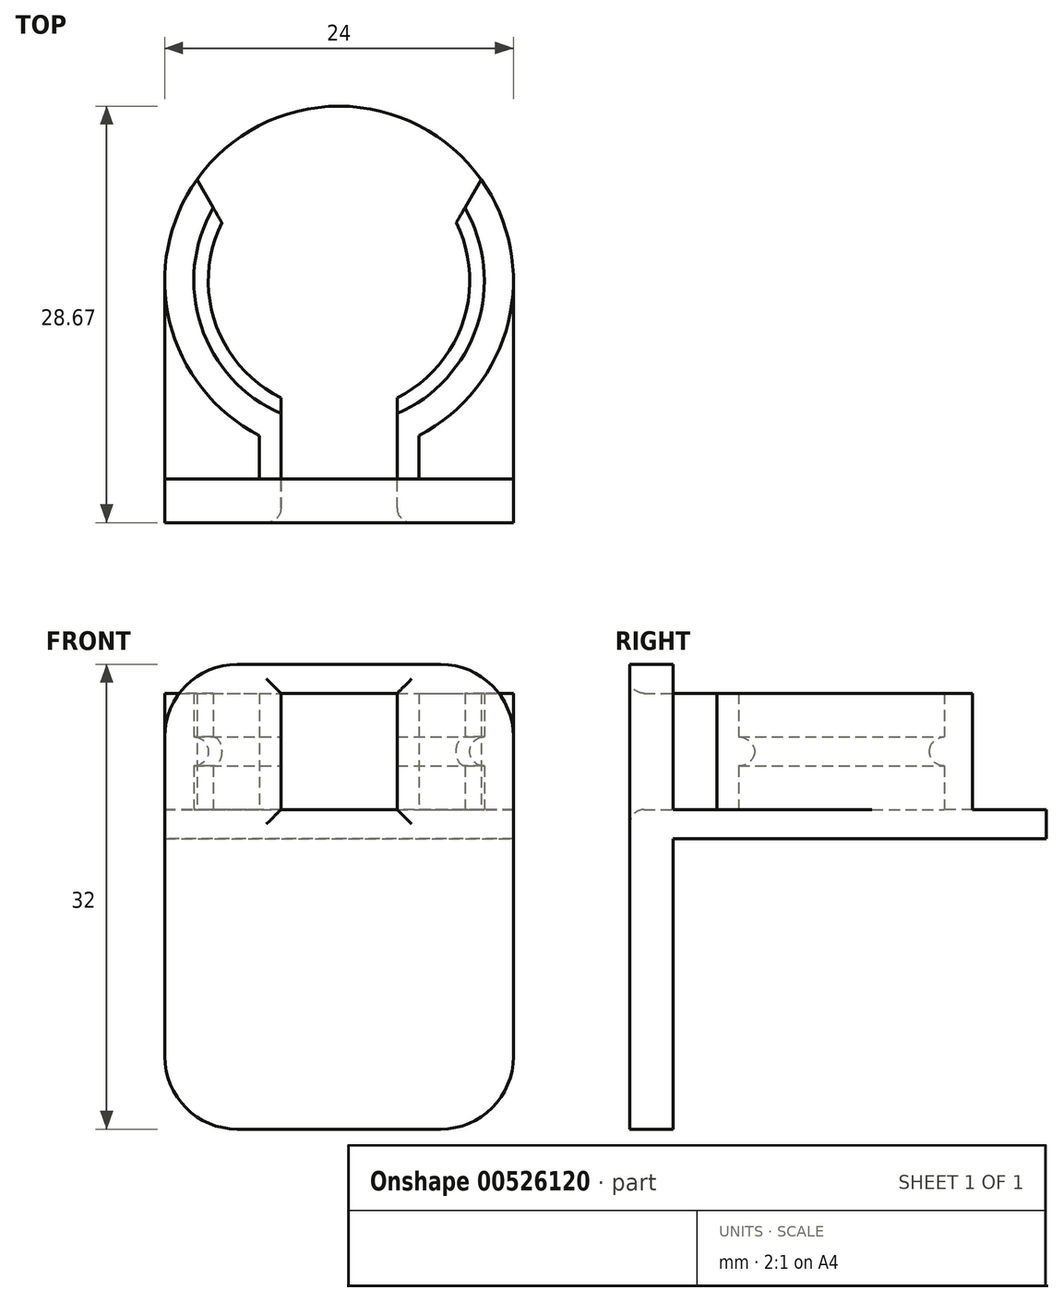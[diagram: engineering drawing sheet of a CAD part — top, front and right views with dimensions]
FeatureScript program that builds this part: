
annotation { "Feature Type Name" : "Feature", "Feature Type Description" : "" }
export const myFeature = defineFeature(function(context is Context, id is Id, definition is map)
    precondition{}
    {
        {
            var Q0;
            Q0=qCreatedBy(makeId("Top.planeOp"),FACE);
            var sketch = newSketch(context, id + "F0", { "sketchPlane" : qUnion([Q0])});
            skArc(sketch, "E0", {"start": v(-5.5, 1.5) * mm, "mid": v(0, 24.17) * mm, "end": v(5.5, 1.5) * mm});
            skArc(sketch, "E1", {"start": v(-5.5, -1.5) * mm, "mid": v(0, -24.17) * mm, "end": v(5.5, -1.5) * mm});
            skLineSegment(sketch, "E2", {"start": v(-5.5, 1.5) * mm, "end": v(-5.5, -1.5) * mm});
            skLineSegment(sketch, "E3", {"start": v(5.5, 1.5) * mm, "end": v(5.5, -1.5) * mm});
            skSolve(sketch);
        }
        {
            var Q0;
            Q0=qSketchRegion(id+"F0",true);
            extrude(context, id + "F1", {"entities" : qUnion([Q0]), "depth" : 2 * mm, "offsetDistance" : 25 * mm});
        }
        {
            var Q0;
            Q0=makeQuery(id+"F1.opExtrude","CAP_FACE",FACE,{"disambiguationData":[OSD([sQuery(id+"F0.wireOp",EDGE,"E0"),sQuery(id+"F0.wireOp",EDGE,"E1"),sQuery(id+"F0.wireOp",EDGE,"E2"),sQuery(id+"F0.wireOp",EDGE,"E3")])],"isStart":false});
            var sketch = newSketch(context, id + "F2", { "sketchPlane" : qUnion([Q0])});
            skArc(sketch, "E4", {"start": v(8.66, 17.17) * mm, "mid": v(9.5, 9.04) * mm, "end": v(4, 3) * mm});
            skArc(sketch, "E5", {"start": v(9.78, 19.11) * mm, "mid": v(11.66, 9.33) * mm, "end": v(5.5, 1.5) * mm});
            skArc(sketch, "E6", {"start": v(-8.66, 17.17) * mm, "mid": v(-9.5, 9.04) * mm, "end": v(-4, 3) * mm});
            skArc(sketch, "E7", {"start": v(5.5, -3.81) * mm, "mid": v(9.59, -9.32) * mm, "end": v(9.17, -16.17) * mm});
            skLineSegment(sketch, "E8", {"start": v(9.78, 19.11) * mm, "end": v(8.66, 17.17) * mm});
            skLineSegment(sketch, "E9", {"start": v(-8.66, 17.17) * mm, "end": v(-9.78, 19.11) * mm});
            skLineSegment(sketch, "E10", {"start": v(5.5, 1.5) * mm, "end": v(5.5, -3.81) * mm});
            skLineSegment(sketch, "E11", {"start": v(-4, 3) * mm, "end": v(-4, -6.24) * mm});
            skLineSegment(sketch, "E12", {"start": v(-4, -6.24) * mm, "end": v(-9.17, -16.17) * mm});
            skLineSegment(sketch, "E13", {"start": v(9.17, -16.17) * mm, "end": v(4, -6.24) * mm});
            skLineSegment(sketch, "E14", {"start": v(4, -6.24) * mm, "end": v(4, 3) * mm});
            skArc(sketch, "E15", {"start": v(-9.78, 19.11) * mm, "mid": v(-11.66, 9.33) * mm, "end": v(-5.5, 1.5) * mm});
            skArc(sketch, "E16", {"start": v(-9.17, -16.17) * mm, "mid": v(-9.59, -9.32) * mm, "end": v(-5.5, -3.81) * mm});
            skLineSegment(sketch, "E17", {"start": v(-5.5, 1.5) * mm, "end": v(-5.5, -3.81) * mm});
            skArc(sketch, "E18.0", {"start": v(-5.5, 1.5) * mm, "mid": v(0, 24.17) * mm, "end": v(5.5, 1.5) * mm, "construction": true});
            skArc(sketch, "E19.0", {"start": v(-5.5, -1.5) * mm, "mid": v(0, -24.17) * mm, "end": v(5.5, -1.5) * mm, "construction": true});
            skSolve(sketch);
        }
        {
            var Q0;
            Q0=qSketchRegion(id+"F2",true);
            extrude(context, id + "F3", {"entities" : qUnion([Q0]), "operationType" : NewBodyOperationType.ADD, "depth" : 3 * mm, "offsetDistance" : 25 * mm});
        }
        {
            var Q0;
            Q0=makeQuery(id+"F3.opExtrude","CAP_FACE",FACE,{"disambiguationData":[OSD([sQuery(id+"F2.wireOp",EDGE,"E4"),sQuery(id+"F2.wireOp",EDGE,"E5"),sQuery(id+"F2.wireOp",EDGE,"E7"),sQuery(id+"F2.wireOp",EDGE,"E8"),sQuery(id+"F2.wireOp",EDGE,"E10"),sQuery(id+"F2.wireOp",EDGE,"E13"),sQuery(id+"F2.wireOp",EDGE,"E14")])],"isStart":false});
            var sketch = newSketch(context, id + "F4", { "sketchPlane" : qUnion([Q0])});
            skArc(sketch, "E20", {"start": v(-9.78, 19.11) * mm, "mid": v(-11.66, 9.33) * mm, "end": v(-5.5, 1.5) * mm});
            skArc(sketch, "E21", {"start": v(9.78, 19.11) * mm, "mid": v(11.66, 9.33) * mm, "end": v(5.5, 1.5) * mm});
            skArc(sketch, "E22", {"start": v(8.07, 16.15) * mm, "mid": v(8.53, 9.28) * mm, "end": v(4, 4.1) * mm});
            skArc(sketch, "E23", {"start": v(-8.07, 16.15) * mm, "mid": v(-8.53, 9.28) * mm, "end": v(-4, 4.1) * mm});
            skArc(sketch, "E24", {"start": v(5.5, -5.04) * mm, "mid": v(8.6, -9.53) * mm, "end": v(8.55, -14.98) * mm});
            skArc(sketch, "E25", {"start": v(-5.5, -5.04) * mm, "mid": v(-8.6, -9.53) * mm, "end": v(-8.55, -14.98) * mm});
            skLineSegment(sketch, "E26", {"start": v(-5.5, 1.5) * mm, "end": v(-5.5, -5.04) * mm});
            skLineSegment(sketch, "E27", {"start": v(5.5, 1.5) * mm, "end": v(5.5, -5.04) * mm});
            skLineSegment(sketch, "E28", {"start": v(-4, 4.1) * mm, "end": v(-4, -6.24) * mm});
            skLineSegment(sketch, "E29", {"start": v(-4, -6.24) * mm, "end": v(-8.55, -14.98) * mm});
            skLineSegment(sketch, "E30", {"start": v(4, 4.1) * mm, "end": v(4, -6.24) * mm});
            skLineSegment(sketch, "E31", {"start": v(4, -6.24) * mm, "end": v(8.55, -14.98) * mm});
            skLineSegment(sketch, "E32", {"start": v(8.07, 16.15) * mm, "end": v(9.78, 19.11) * mm});
            skLineSegment(sketch, "E33", {"start": v(-9.78, 19.11) * mm, "end": v(-8.07, 16.15) * mm});
            skLineSegment(sketch, "E34.0", {"start": v(-8.66, 17.17) * mm, "end": v(-9.78, 19.11) * mm, "construction": true});
            skLineSegment(sketch, "E35.0", {"start": v(9.78, 19.11) * mm, "end": v(8.66, 17.17) * mm, "construction": true});
            skLineSegment(sketch, "E36.0", {"start": v(-4, -6.24) * mm, "end": v(-9.17, -16.17) * mm, "construction": true});
            skLineSegment(sketch, "E37.0", {"start": v(9.17, -16.17) * mm, "end": v(4, -6.24) * mm, "construction": true});
            skArc(sketch, "E38.0", {"start": v(-9.78, 19.11) * mm, "mid": v(0, 24.17) * mm, "end": v(9.78, 19.11) * mm, "construction": true});
            skArc(sketch, "E39.0", {"start": v(-5.5, -1.5) * mm, "mid": v(0, -24.17) * mm, "end": v(5.5, -1.5) * mm, "construction": true});
            skSolve(sketch);
        }
        {
            var Q0;
            Q0=qSketchRegion(id+"F4",true);
            extrude(context, id + "F5", {"entities" : qUnion([Q0]), "operationType" : NewBodyOperationType.ADD, "depth" : 2 * mm, "offsetDistance" : 25 * mm});
        }
        {
            var Q0;
            Q0=makeQuery(id+"F5.opExtrude","CAP_FACE",FACE,{"disambiguationData":[OSD([sQuery(id+"F4.wireOp",EDGE,"E21"),sQuery(id+"F4.wireOp",EDGE,"E22"),sQuery(id+"F4.wireOp",EDGE,"E24"),sQuery(id+"F4.wireOp",EDGE,"E27"),sQuery(id+"F4.wireOp",EDGE,"E30"),sQuery(id+"F4.wireOp",EDGE,"E31"),sQuery(id+"F4.wireOp",EDGE,"E32")])],"isStart":false});
            var sketch = newSketch(context, id + "F6", { "sketchPlane" : qUnion([Q0])});
            skArc(sketch, "E40", {"start": v(8.66, 17.17) * mm, "mid": v(9.5, 9.04) * mm, "end": v(4, 3) * mm});
            skArc(sketch, "E41", {"start": v(9.78, 19.11) * mm, "mid": v(11.66, 9.33) * mm, "end": v(5.5, 1.5) * mm});
            skArc(sketch, "E42", {"start": v(-8.66, 17.17) * mm, "mid": v(-9.5, 9.04) * mm, "end": v(-4, 3) * mm});
            skArc(sketch, "E43", {"start": v(5.5, -3.81) * mm, "mid": v(9.59, -9.32) * mm, "end": v(9.17, -16.17) * mm});
            skLineSegment(sketch, "E44", {"start": v(9.78, 19.11) * mm, "end": v(8.66, 17.17) * mm});
            skLineSegment(sketch, "E45", {"start": v(-8.66, 17.17) * mm, "end": v(-9.78, 19.11) * mm});
            skLineSegment(sketch, "E46", {"start": v(5.5, 1.5) * mm, "end": v(5.5, -3.81) * mm});
            skLineSegment(sketch, "E47", {"start": v(-4, 3) * mm, "end": v(-4, -6.24) * mm});
            skLineSegment(sketch, "E48", {"start": v(-4, -6.24) * mm, "end": v(-9.17, -16.17) * mm});
            skLineSegment(sketch, "E49", {"start": v(9.17, -16.17) * mm, "end": v(4, -6.24) * mm});
            skLineSegment(sketch, "E50", {"start": v(4, -6.24) * mm, "end": v(4, 3) * mm});
            skArc(sketch, "E51", {"start": v(-9.78, 19.11) * mm, "mid": v(-11.66, 9.33) * mm, "end": v(-5.5, 1.5) * mm});
            skArc(sketch, "E52", {"start": v(-9.17, -16.17) * mm, "mid": v(-9.59, -9.32) * mm, "end": v(-5.5, -3.81) * mm});
            skLineSegment(sketch, "E53", {"start": v(-5.5, 1.5) * mm, "end": v(-5.5, -3.81) * mm});
            skArc(sketch, "E54.0", {"start": v(-5.5, -1.5) * mm, "mid": v(0, -24.17) * mm, "end": v(5.5, -1.5) * mm, "construction": true});
            skArc(sketch, "E55.0", {"start": v(-9.78, 19.11) * mm, "mid": v(0, 24.17) * mm, "end": v(9.78, 19.11) * mm, "construction": true});
            skSolve(sketch);
        }
        {
            var Q0;
            Q0=qSketchRegion(id+"F6",true);
            extrude(context, id + "F7", {"entities" : qUnion([Q0]), "operationType" : NewBodyOperationType.ADD, "depth" : 3 * mm, "offsetDistance" : 25 * mm});
        }
        {
            var Q0;
            Q0=makeQuery(id+"F5.opExtrude","CAP_EDGE",EDGE,{"disambiguationData":[OSD([sQuery(id+"F4.wireOp",EDGE,"E22")])],"isStart":false});
            var Q1;
            Q1=makeQuery(id+"F5.opExtrude","CAP_EDGE",EDGE,{"disambiguationData":[OSD([sQuery(id+"F4.wireOp",EDGE,"E23")])],"isStart":false});
            var Q2;
            Q2=makeQuery(id+"F5.opExtrude","CAP_EDGE",EDGE,{"disambiguationData":[OSD([sQuery(id+"F4.wireOp",EDGE,"E23")])],"isStart":true});
            var Q3;
            Q3=makeQuery(id+"F5.opExtrude","CAP_EDGE",EDGE,{"disambiguationData":[OSD([sQuery(id+"F4.wireOp",EDGE,"E22")])],"isStart":true});
            var Q4;
            Q4=makeQuery(id+"F5.opExtrude","CAP_EDGE",EDGE,{"disambiguationData":[OSD([sQuery(id+"F4.wireOp",EDGE,"E25")])],"isStart":true});
            var Q5;
            Q5=makeQuery(id+"F5.opExtrude","CAP_EDGE",EDGE,{"disambiguationData":[OSD([sQuery(id+"F4.wireOp",EDGE,"E25")])],"isStart":false});
            var Q6;
            Q6=makeQuery(id+"F5.opExtrude","CAP_EDGE",EDGE,{"disambiguationData":[OSD([sQuery(id+"F4.wireOp",EDGE,"E24")])],"isStart":false});
            var Q7;
            Q7=makeQuery(id+"F5.opExtrude","CAP_EDGE",EDGE,{"disambiguationData":[OSD([sQuery(id+"F4.wireOp",EDGE,"E24")])],"isStart":true});
            fillet(context, id + "F8", {"entities" : qUnion([Q0, Q1, Q2, Q3, Q4, Q5, Q6, Q7]), "radius" : 1 * mm, "tangentPropagation" : true, "allowEdgeOverflow" : false});
        }
        {
            var Q0;
            Q0=makeQuery(id+"F7.opExtrude","CAP_FACE",FACE,{"disambiguationData":[OSD([sQuery(id+"F6.wireOp",EDGE,"E40"),sQuery(id+"F6.wireOp",EDGE,"E41"),sQuery(id+"F6.wireOp",EDGE,"E43"),sQuery(id+"F6.wireOp",EDGE,"E44"),sQuery(id+"F6.wireOp",EDGE,"E46"),sQuery(id+"F6.wireOp",EDGE,"E49"),sQuery(id+"F6.wireOp",EDGE,"E50")])],"isStart":false});
            var sketch = newSketch(context, id + "F9", { "sketchPlane" : qUnion([Q0])});
            skLineSegment(sketch, "E56.bottom", {"start": v(-12, -1.5) * mm, "end": v(12, -1.5) * mm});
            skLineSegment(sketch, "E56.top", {"start": v(-12, -24.17) * mm, "end": v(12, -24.17) * mm});
            skLineSegment(sketch, "E56.left", {"start": v(-12, -1.5) * mm, "end": v(-12, -24.17) * mm});
            skLineSegment(sketch, "E56.right", {"start": v(12, -1.5) * mm, "end": v(12, -24.17) * mm});
            skSolve(sketch);
        }
        {
            var Q0;
            Q0=qSketchRegion(id+"F9",true);
            extrude(context, id + "F10", {"entities" : qUnion([Q0]), "operationType" : NewBodyOperationType.REMOVE, "oppositeDirection" : true, "depth" : 10 * mm, "offsetDistance" : 25 * mm});
        }
        {
            var Q0;
            Q0=makeQuery(id+"F10.boolean.opBoolean","COPY",FACE,{"derivedFrom":makeQuery(id+"F10.opExtrude","SWEPT_FACE",FACE,{"disambiguationData":[OSD([sQuery(id+"F9.wireOp",EDGE,"E56.bottom")])]})});
            var sketch = newSketch(context, id + "F11", { "sketchPlane" : qUnion([Q0])});
            skLineSegment(sketch, "E57.bottom", {"start": v(-12, -20) * mm, "end": v(12, -20) * mm});
            skLineSegment(sketch, "E57.top", {"start": v(-12, 12) * mm, "end": v(12, 12) * mm});
            skLineSegment(sketch, "E57.left", {"start": v(-12, 12) * mm, "end": v(-12, -20) * mm});
            skLineSegment(sketch, "E57.right", {"start": v(12, 12) * mm, "end": v(12, -20) * mm});
            skLineSegment(sketch, "E58.bottom", {"start": v(-4, 10) * mm, "end": v(4, 10) * mm});
            skLineSegment(sketch, "E58.top", {"start": v(-4, 2) * mm, "end": v(4, 2) * mm});
            skLineSegment(sketch, "E58.left", {"start": v(-4, 10) * mm, "end": v(-4, 2) * mm});
            skLineSegment(sketch, "E58.right", {"start": v(4, 10) * mm, "end": v(4, 2) * mm});
            skSolve(sketch);
        }
        {
            var Q0;
            Q0=qSketchRegion(id+"F11",true);
            extrude(context, id + "F12", {"entities" : qUnion([Q0]), "operationType" : NewBodyOperationType.ADD, "depth" : 3 * mm, "offsetDistance" : 25 * mm});
        }
        {
            var Q0;
            Q0=makeQuery(id+"F12.opExtrude","CAP_EDGE",EDGE,{"disambiguationData":[OSD([sQuery(id+"F11.wireOp",EDGE,"E58.bottom")])],"isStart":false});
            var Q1;
            Q1=makeQuery(id+"F12.opExtrude","CAP_EDGE",EDGE,{"disambiguationData":[OSD([sQuery(id+"F11.wireOp",EDGE,"E58.right")])],"isStart":false});
            var Q2;
            Q2=makeQuery(id+"F12.opExtrude","CAP_EDGE",EDGE,{"disambiguationData":[OSD([sQuery(id+"F11.wireOp",EDGE,"E58.left")])],"isStart":false});
            var Q3;
            Q3=makeQuery(id+"F12.opExtrude","CAP_EDGE",EDGE,{"disambiguationData":[OSD([sQuery(id+"F11.wireOp",EDGE,"E58.top")])],"isStart":false});
            fillet(context, id + "F13", {"entities" : qUnion([Q0, Q1, Q2, Q3]), "radius" : 1 * mm, "tangentPropagation" : true, "allowEdgeOverflow" : false});
        }
        {
            var Q0;
            Q0=makeQuery(id+"F12.opExtrude","SWEPT_EDGE",EDGE,{"disambiguationData":[OSD([sQuery(id+"F11.wireOp",EDGE,"E57.top"),sQuery(id+"F11.wireOp",EDGE,"E57.left")])]});
            var Q1;
            Q1=makeQuery(id+"F12.opExtrude","SWEPT_EDGE",EDGE,{"disambiguationData":[OSD([sQuery(id+"F11.wireOp",EDGE,"E57.top"),sQuery(id+"F11.wireOp",EDGE,"E57.right")])]});
            var Q2;
            Q2=makeQuery(id+"F12.opExtrude","SWEPT_EDGE",EDGE,{"disambiguationData":[OSD([sQuery(id+"F11.wireOp",EDGE,"E57.bottom"),sQuery(id+"F11.wireOp",EDGE,"E57.right")])]});
            var Q3;
            Q3=makeQuery(id+"F12.opExtrude","SWEPT_EDGE",EDGE,{"disambiguationData":[OSD([sQuery(id+"F11.wireOp",EDGE,"E57.bottom"),sQuery(id+"F11.wireOp",EDGE,"E57.left")])]});
            fillet(context, id + "F14", {"entities" : qUnion([Q0, Q1, Q2, Q3]), "radius" : 5 * mm, "tangentPropagation" : true, "allowEdgeOverflow" : false});
        }
        {
            var Q0;
            Q0=makeQuery(id+"F1.opExtrude","CAP_FACE",FACE,{"disambiguationData":[OSD([sQuery(id+"F0.wireOp",EDGE,"E0"),sQuery(id+"F0.wireOp",EDGE,"E1"),sQuery(id+"F0.wireOp",EDGE,"E2"),sQuery(id+"F0.wireOp",EDGE,"E3")])],"isStart":true});
            var sketch = newSketch(context, id + "F15", { "sketchPlane" : qUnion([Q0])});
            skLineSegment(sketch, "E59.bottom", {"start": v(-12, 1.5) * mm, "end": v(12, 1.5) * mm});
            skLineSegment(sketch, "E59.top", {"start": v(-12, -12.17) * mm, "end": v(12, -12.17) * mm});
            skLineSegment(sketch, "E59.left", {"start": v(-12, 1.5) * mm, "end": v(-12, -12.17) * mm});
            skLineSegment(sketch, "E59.right", {"start": v(12, 1.5) * mm, "end": v(12, -12.17) * mm});
            skSolve(sketch);
        }
        {
            var Q0;
            Q0 = qSketchRegion(id + "F15", true);
            extrude(context, id + "F16", {"entities" : qUnion([Q0]), "operationType" : NewBodyOperationType.ADD, "oppositeDirection" : true, "depth" : 2 * mm, "offsetDistance" : 25 * mm});
        }
    });
